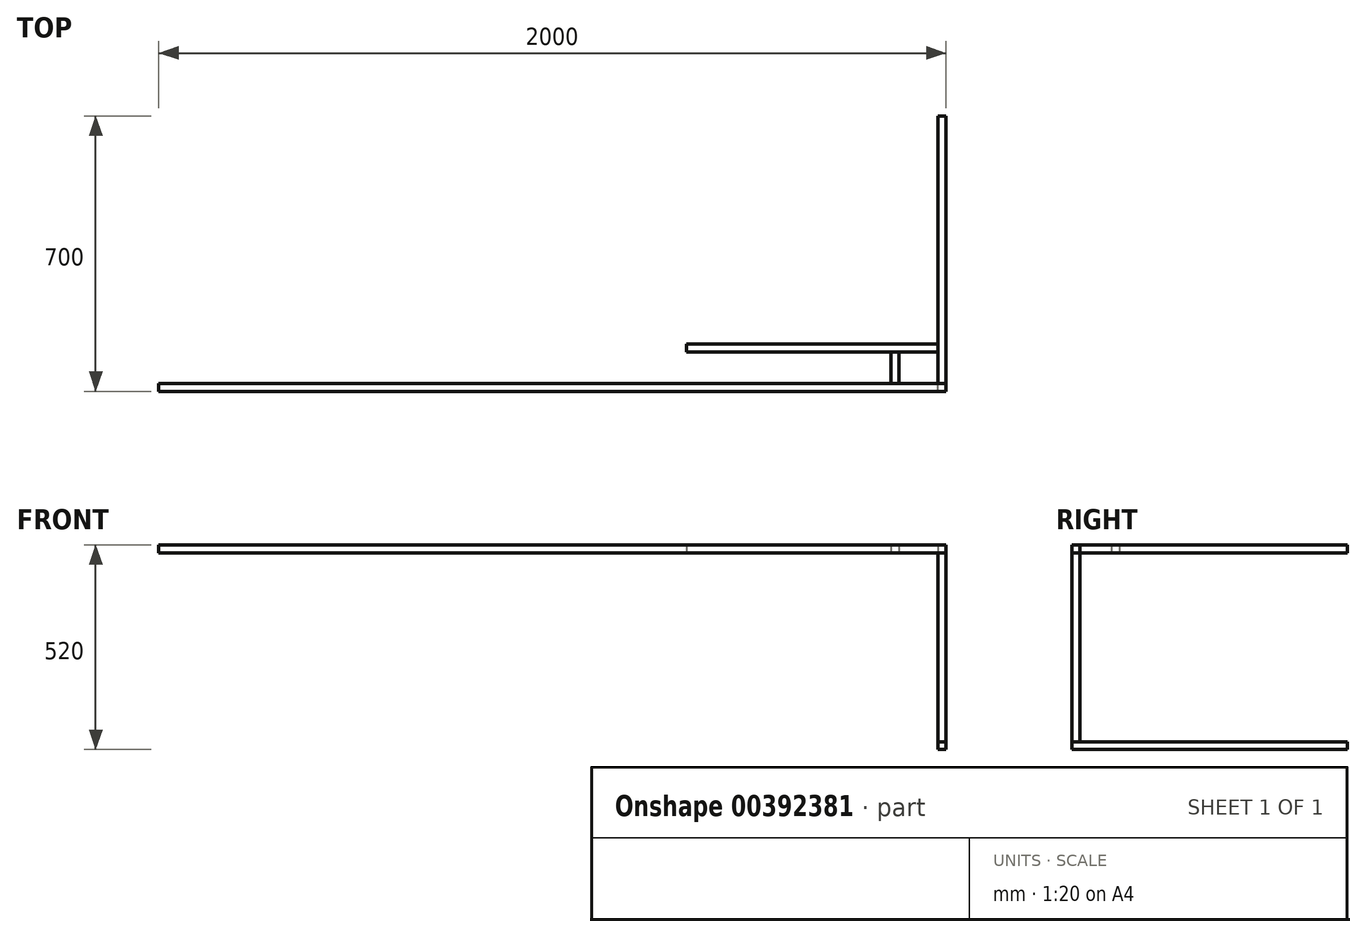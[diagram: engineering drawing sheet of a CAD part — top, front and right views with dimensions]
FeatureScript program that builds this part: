
annotation { "Feature Type Name" : "Feature", "Feature Type Description" : "" }
export const myFeature = defineFeature(function(context is Context, id is Id, definition is map)
    precondition{}
    {
        {
            var Q0;
            Q0=qCreatedBy(makeId("Front.planeOp"),FACE);
            var sketch = newSketch(context, id + "F0", { "sketchPlane" : qUnion([Q0])});
            skLineSegment(sketch, "E0.bottom", {"start": v(0, 0) * mm, "end": v(-2000, 0) * mm});
            skLineSegment(sketch, "E0.top", {"start": v(0, -20) * mm, "end": v(-2000, -20) * mm});
            skLineSegment(sketch, "E0.left", {"start": v(0, -20) * mm, "end": v(0, 0) * mm});
            skLineSegment(sketch, "E0.right", {"start": v(-2000, -20) * mm, "end": v(-2000, 0) * mm});
            skSolve(sketch);
        }
        {
            var Q0;
            Q0=qSketchRegion(id+"F0",true);
            extrude(context, id + "F1", {"entities" : qUnion([Q0]), "oppositeDirection" : true, "depth" : 20 * mm});
        }
        {
            var Q0;
            Q0=makeQuery(id+"F1.opExtrude","CAP_FACE",FACE,{"disambiguationData":[OSD([sQuery(id+"F0.wireOp",EDGE,"E0.bottom"),sQuery(id+"F0.wireOp",EDGE,"E0.top"),sQuery(id+"F0.wireOp",EDGE,"E0.left"),sQuery(id+"F0.wireOp",EDGE,"E0.right")])],"isStart":false});
            var sketch = newSketch(context, id + "F2", { "sketchPlane" : qUnion([Q0])});
            skLineSegment(sketch, "E1.bottom", {"start": v(0, 0) * mm, "end": v(20, 0) * mm});
            skLineSegment(sketch, "E1.top", {"start": v(0, -20) * mm, "end": v(20, -20) * mm});
            skLineSegment(sketch, "E1.left", {"start": v(0, 0) * mm, "end": v(0, -20) * mm});
            skLineSegment(sketch, "E1.right", {"start": v(20, 0) * mm, "end": v(20, -20) * mm});
            skSolve(sketch);
        }
        {
            var Q0;
            Q0=qSketchRegion(id+"F2",true);
            extrude(context, id + "F3", {"entities" : qUnion([Q0]), "depth" : 680 * mm});
        }
        {
            var Q0;
            Q0=makeQuery(id+"F1.opExtrude","SWEPT_FACE",FACE,{"disambiguationData":[OSD([sQuery(id+"F0.wireOp",EDGE,"E0.top")])]});
            var sketch = newSketch(context, id + "F4", { "sketchPlane" : qUnion([Q0])});
            skLineSegment(sketch, "E2.bottom", {"start": v(0, 0) * mm, "end": v(-20, 0) * mm});
            skLineSegment(sketch, "E2.top", {"start": v(0, -20) * mm, "end": v(-20, -20) * mm});
            skLineSegment(sketch, "E2.left", {"start": v(0, 0) * mm, "end": v(0, -20) * mm});
            skLineSegment(sketch, "E2.right", {"start": v(-20, 0) * mm, "end": v(-20, -20) * mm});
            skSolve(sketch);
        }
        {
            var Q0;
            Q0=qSketchRegion(id+"F4",true);
            extrude(context, id + "F5", {"entities" : qUnion([Q0]), "depth" : 480 * mm});
        }
        {
            var Q0;
            Q0=makeQuery(id+"F5.opExtrude","SWEPT_FACE",FACE,{"disambiguationData":[OSD([sQuery(id+"F4.wireOp",EDGE,"E2.bottom")])]});
            var sketch = newSketch(context, id + "F6", { "sketchPlane" : qUnion([Q0])});
            skLineSegment(sketch, "E3.bottom", {"start": v(0, -500) * mm, "end": v(-20, -500) * mm});
            skLineSegment(sketch, "E3.top", {"start": v(0, -520) * mm, "end": v(-20, -520) * mm});
            skLineSegment(sketch, "E3.left", {"start": v(0, -500) * mm, "end": v(0, -520) * mm});
            skLineSegment(sketch, "E3.right", {"start": v(-20, -500) * mm, "end": v(-20, -520) * mm});
            skSolve(sketch);
        }
        {
            var Q0;
            Q0=qSketchRegion(id+"F6",true);
            var Q1;
            Q1=makeQuery(id+"F3.opExtrude","CAP_FACE",FACE,{"disambiguationData":[OSD([sQuery(id+"F2.wireOp",EDGE,"E1.bottom"),sQuery(id+"F2.wireOp",EDGE,"E1.top"),sQuery(id+"F2.wireOp",EDGE,"E1.left"),sQuery(id+"F2.wireOp",EDGE,"E1.right")])],"isStart":false});
            extrude(context, id + "F7", {"entities" : qUnion([Q0]), "endBound" : BoundingType.UP_TO_SURFACE, "oppositeDirection" : true, "endBoundEntityFace" : qUnion([Q1]), "depth" : 25 * mm});
        }
        {
            var Q0;
            Q0=makeQuery(id+"F3.opExtrude","SWEPT_FACE",FACE,{"disambiguationData":[OSD([sQuery(id+"F2.wireOp",EDGE,"E1.right")])]});
            var sketch = newSketch(context, id + "F8", { "sketchPlane" : qUnion([Q0])});
            skLineSegment(sketch, "E4.bottom", {"start": v(-100, 0) * mm, "end": v(-120, 0) * mm});
            skLineSegment(sketch, "E4.top", {"start": v(-100, -20) * mm, "end": v(-120, -20) * mm});
            skLineSegment(sketch, "E4.left", {"start": v(-100, 0) * mm, "end": v(-100, -20) * mm});
            skLineSegment(sketch, "E4.right", {"start": v(-120, 0) * mm, "end": v(-120, -20) * mm});
            skSolve(sketch);
        }
        {
            var Q0;
            Q0=qSketchRegion(id+"F8",true);
            extrude(context, id + "F9", {"entities" : qUnion([Q0]), "depth" : 640 * mm});
        }
        {
            var Q0;
            Q0=makeQuery(id+"F1.opExtrude","CAP_FACE",FACE,{"disambiguationData":[OSD([sQuery(id+"F0.wireOp",EDGE,"E0.bottom"),sQuery(id+"F0.wireOp",EDGE,"E0.top"),sQuery(id+"F0.wireOp",EDGE,"E0.left"),sQuery(id+"F0.wireOp",EDGE,"E0.right")])],"isStart":false});
            var sketch = newSketch(context, id + "F10", { "sketchPlane" : qUnion([Q0])});
            skLineSegment(sketch, "E5.bottom", {"start": v(140, -20) * mm, "end": v(120, -20) * mm});
            skLineSegment(sketch, "E5.top", {"start": v(140, 0) * mm, "end": v(120, 0) * mm});
            skLineSegment(sketch, "E5.left", {"start": v(140, -20) * mm, "end": v(140, 0) * mm});
            skLineSegment(sketch, "E5.right", {"start": v(120, -20) * mm, "end": v(120, 0) * mm});
            skSolve(sketch);
        }
        {
            var Q0;
            Q0 = qSketchRegion(id + "F10", true);
            var Q1;
            Q1=makeQuery(id+"F9.opExtrude","SWEPT_FACE",FACE,{"disambiguationData":[OSD([sQuery(id+"F8.wireOp",EDGE,"E4.left")])]});
            extrude(context, id + "F11", {"entities" : qUnion([Q0]), "endBound" : BoundingType.UP_TO_SURFACE, "endBoundEntityFace" : qUnion([Q1]), "depth" : 25 * mm});
        }
    });
